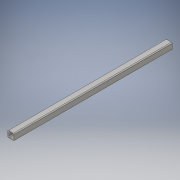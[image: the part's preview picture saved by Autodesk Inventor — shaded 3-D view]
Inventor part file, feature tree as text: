
AUTODESK INVENTOR PART (.ipt)
format: ipt  version: 2016 (Build 200138000, 138)  size: 113,664 bytes
history: native  units: in
note: dims shown in document units (in); Inventor stores cm internally (conversion verified against a paired STEP export)
features: extrude x1, sketch x1
ambient origin geometry x8: Origin, YZ Plane, XZ Plane, XY Plane, X Axis, Y Axis, Z Axis, Center Point
bodies: Solid1 (feature_tree)
feature tree (2):
  extrude  "Extrusion1"  Depth=1.0in
  sketch  "Sketch1"  dims[d0=1.0in d1=1.0in d2=0.125in d3=0.125in d4=24.0in d5=0.0in]
